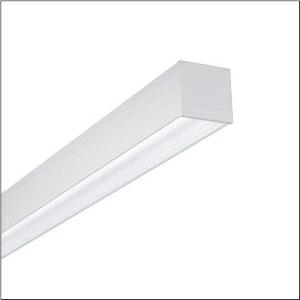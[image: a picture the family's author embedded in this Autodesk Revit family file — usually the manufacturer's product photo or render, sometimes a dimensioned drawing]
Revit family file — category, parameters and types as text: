
# Revit family: silica_r_5mx22wd1e4a_75c3
name_source: partatom
category: Lighting Fixtures
units: mm (PartAtom-declared; Revit-internal decimal feet)

## family parameters
Cut with Voids When Loaded = No
Host = Face
Light Source = No
Part Type = Normal
Room Calculation Point = No
Round Connector Dimension = Use Diameter
Shared = No

## types (1)
- --- (1 x LED, 4680 lm, 29.3 W, 4000K)
    Apparent Load = 29 VA
    CIE Flux Codes = 70 95 99 100 100
    Color Rendering = 80
    Color Temperature = 4000K
    Default Elevation = 1800 mm
    Description = Silica®, office luminaire, primary light control with wallwasher, of aluminium, light emission: direct distribution, primary light characteristic: asymmetric, installation type: surface-mounted, LED rated luminous flux: 4.680 lm, light colour: 840, colour temperature: 4000K, control gear: ECG DALI, with terminal, 3+2-pole, max. 2.5mm², mains connection: 230V, AC, 50/60Hz, rated input power: 29W, luminaire housing, of aluminium, anodised, silver, length: 1.440 mm, width: 64 mm, height: 64mm, protection rating (complete): IP20, insulation class (complete): insulation class I (protective earthing), certification: CE, permissible ambient temperature for indoor applications: 0..+35°C, standard: EN 50419, packaging unit: 1 piece
    Height = 64 mm
    Lamp = 1 x LED
    Lamp Light Flux = 4680 lm
    Lamp Power = 29.3 W
    Lamp count = 1
    Length = 1442 mm
    Luminous efficacy = 160 lm/W
    Manufacturer = Siteco
    ModVariant = No
    Model = 5MX22WD1E4A
    Mounting Place = Ceiling
    Mounting Type = Surface mounted
    Number of Poles = 1
    OnlyDefault = Yes
    Power Factor = 1
    Product Name = Silica®
    Product group = office luminaire | ceiling mounted
    ProductGroupID = 302
    Protection Class = Protection class I
    Protection Degree = IP 20
    RLX_Detail_Level = 1
    RlxData = <blob elided: 27881 chars, md5=63f6b6ae>
    Socket = socket
    Standby Power = 0 W
    System Light Flux = 4680 lm
    System Power = 29 W
    Type Comments = factory setting: luminous flux: 100 % | dim-lin: 254 | 164 mA
    Type Image = l_1004827.jpg
    URL = http://relux.com
    VarID = @adj_131728
    Voltage = 0 V
    Weight = 0.00 kg
    Width = 66 mm

## geometry (parser evidence)
native form markers: Blend x4, Sweep x10
no freeform markers — native parametric forms only
